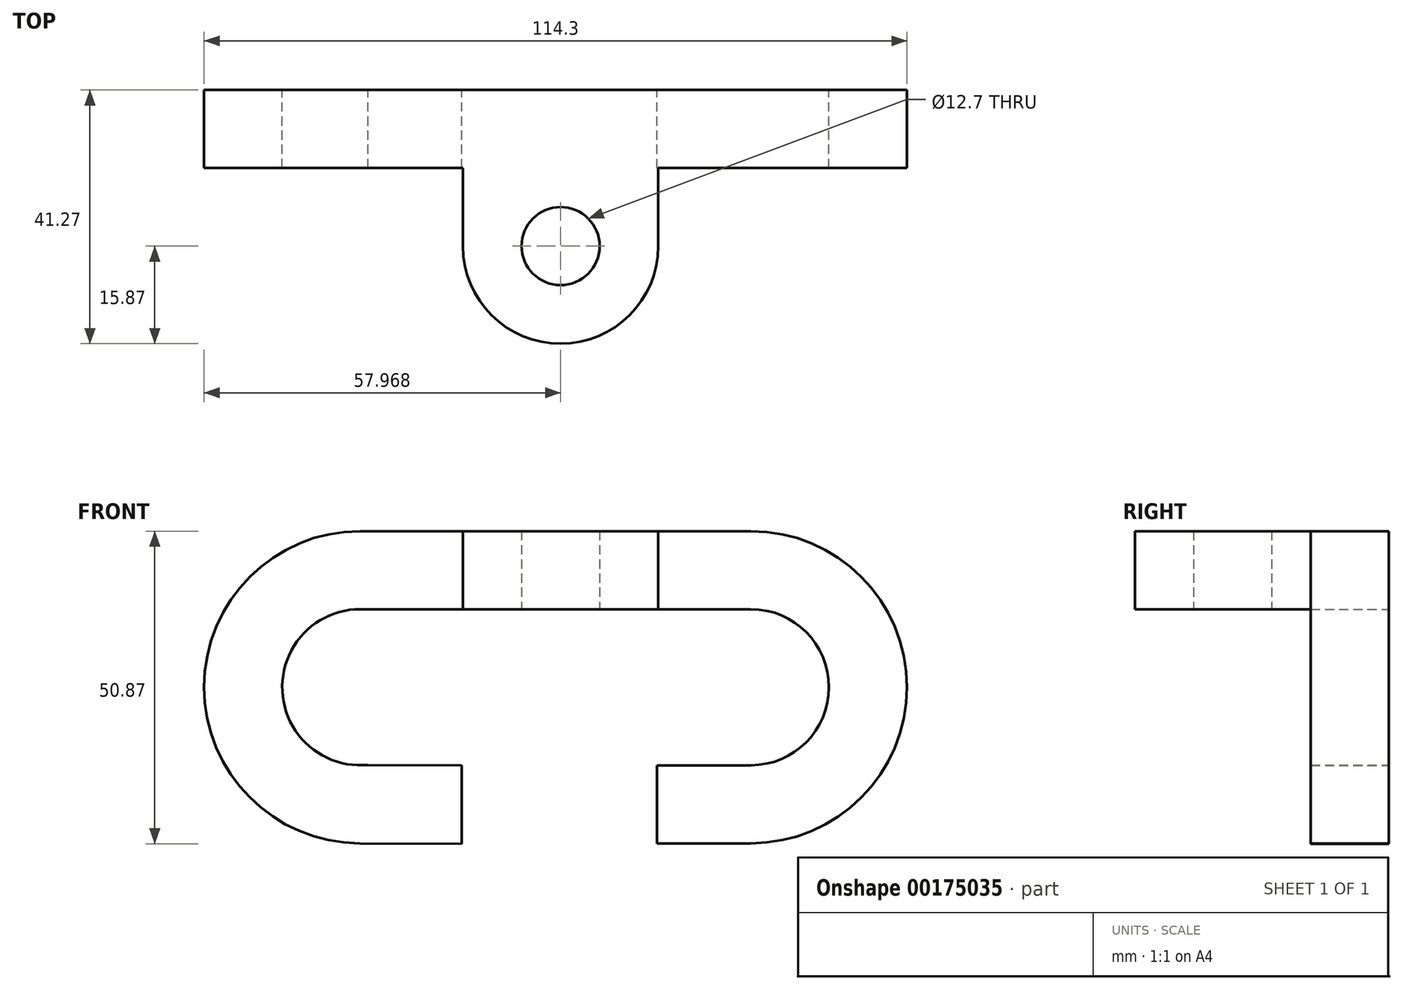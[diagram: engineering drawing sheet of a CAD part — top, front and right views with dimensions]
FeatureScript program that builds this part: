
annotation { "Feature Type Name" : "Feature", "Feature Type Description" : "" }
export const myFeature = defineFeature(function(context is Context, id is Id, definition is map)
    precondition{}
    {
        {
            var Q0;
            Q0=qCreatedBy(makeId("Front.planeOp"),FACE);
            var sketch = newSketch(context, id + "F0", { "sketchPlane" : qUnion([Q0])});
            skArc(sketch, "E0", {"start": v(-45.27, 32) * mm, "mid": v(-70.67, 6.66) * mm, "end": v(-45.38, -18.8) * mm});
            skLineSegment(sketch, "E1", {"start": v(-45.27, 32) * mm, "end": v(18.23, 32) * mm});
            skArc(sketch, "E2", {"start": v(18.23, -18.8) * mm, "mid": v(43.63, 6.6) * mm, "end": v(18.23, 32) * mm});
            skArc(sketch, "E3", {"start": v(-45.27, 19.3) * mm, "mid": v(-57.95, 5.97) * mm, "end": v(-44, -6.03) * mm});
            skArc(sketch, "E4", {"start": v(18.23, -6.1) * mm, "mid": v(30.93, 6.6) * mm, "end": v(18.23, 19.3) * mm});
            skLineSegment(sketch, "E5", {"start": v(-45.27, 19.3) * mm, "end": v(18.23, 19.3) * mm});
            skLineSegment(sketch, "E6", {"start": v(-44, -6.03) * mm, "end": v(-28.76, -6.1) * mm});
            skLineSegment(sketch, "E7", {"start": v(-45.38, -18.8) * mm, "end": v(-28.76, -18.86) * mm});
            skLineSegment(sketch, "E8", {"start": v(-28.76, -18.86) * mm, "end": v(-28.76, -6.1) * mm});
            skLineSegment(sketch, "E9", {"start": v(18.23, -6.1) * mm, "end": v(2.99, -6.1) * mm});
            skLineSegment(sketch, "E10", {"start": v(2.99, -6.1) * mm, "end": v(2.99, -18.8) * mm});
            skLineSegment(sketch, "E11", {"start": v(2.99, -18.8) * mm, "end": v(18.23, -18.8) * mm});
            skSolve(sketch);
        }
        {
            var Q0;
            Q0 = qSketchRegion(id + "F0", true);
            extrude(context, id + "F1", {"entities" : qUnion([Q0]), "depth" : 12.7 * mm});
        }
        {
            var Q0;
            Q0=makeQuery(id+"F1.opExtrude","SWEPT_FACE",FACE,{"disambiguationData":[OSD([sQuery(id+"F0.wireOp",EDGE,"E5")])]});
            var sketch = newSketch(context, id + "F2", { "sketchPlane" : qUnion([Q0])});
            skArc(sketch, "E12", {"start": v(3.17, 25.4) * mm, "mid": v(-12.7, 41.28) * mm, "end": v(-28.58, 25.4) * mm});
            skLineSegment(sketch, "E13", {"start": v(-28.58, 25.4) * mm, "end": v(-28.58, 12.7) * mm});
            skLineSegment(sketch, "E14", {"start": v(3.17, 25.4) * mm, "end": v(3.17, 12.7) * mm});
            skCircle(sketch, "E15", {"center": v(-12.7, 25.4) * mm, "radius": 6.35 * mm});
            skSolve(sketch);
        }
        {
            var Q0;
            Q0=makeQuery(id+"F2.imprint","IMPRINT",FACE,{"disambiguationData":[TD([[makeQuery(id+"F2.imprint","IMPRINT",EDGE,{"derivedFrom":sQuery(id+"F2.wireOp",EDGE,"E12")}),1.0]])]});
            extrude(context, id + "F3", {"entities" : qUnion([Q0]), "operationType" : NewBodyOperationType.ADD, "oppositeDirection" : true, "depth" : 12.7 * mm});
        }
    });
